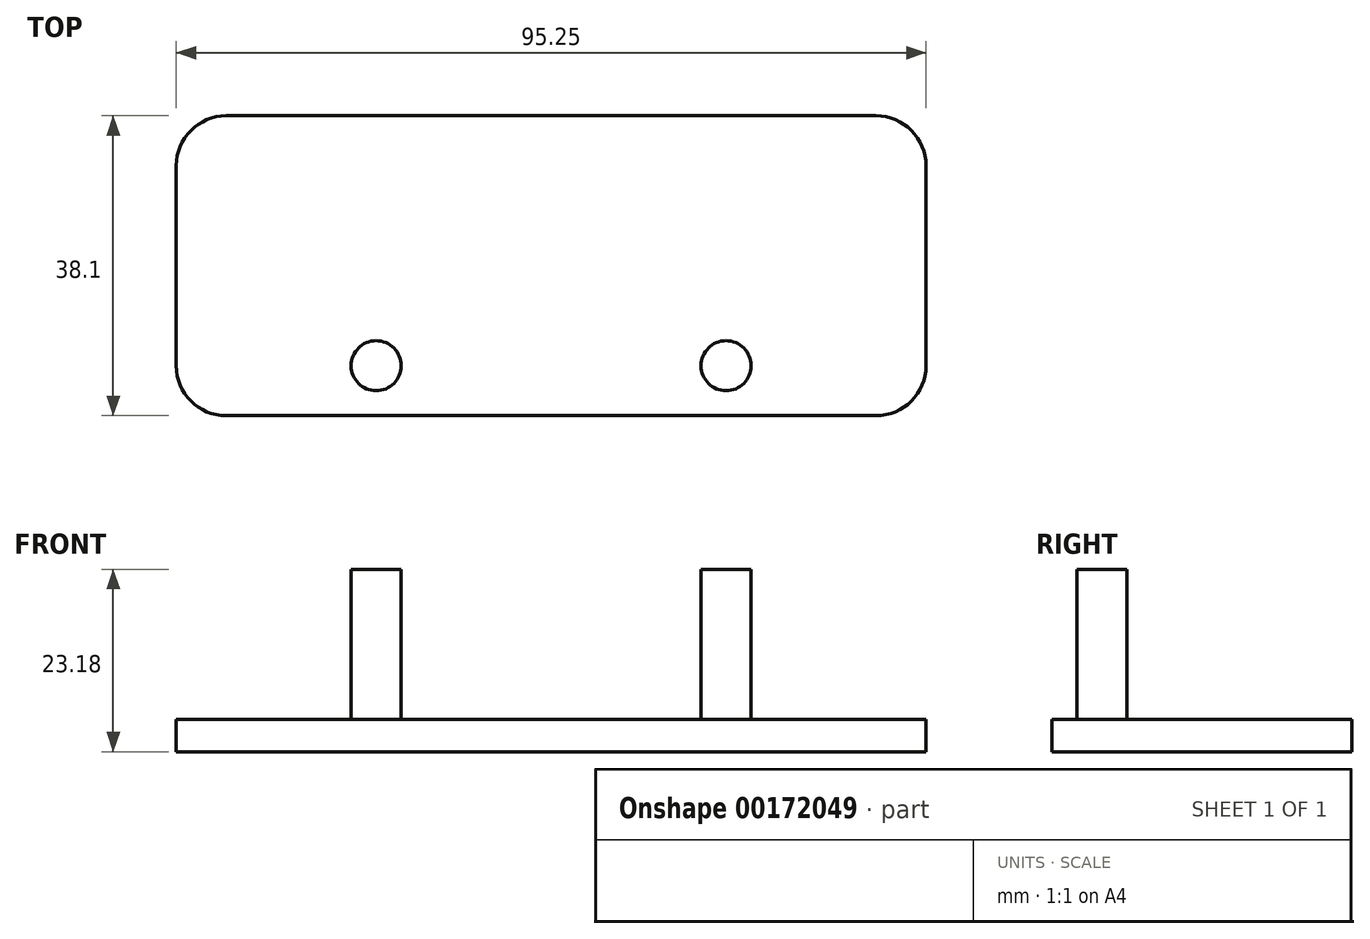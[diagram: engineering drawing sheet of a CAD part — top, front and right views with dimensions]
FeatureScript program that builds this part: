
annotation { "Feature Type Name" : "Feature", "Feature Type Description" : "" }
export const myFeature = defineFeature(function(context is Context, id is Id, definition is map)
    precondition{}
    {
        {
            var Q0;
            Q0=qCreatedBy(makeId("Top.planeOp"),FACE);
            var sketch = newSketch(context, id + "F0", { "sketchPlane" : qUnion([Q0])});
            skLineSegment(sketch, "E0.bottom", {"start": v(6.35, 0) * mm, "end": v(88.9, 0) * mm});
            skLineSegment(sketch, "E0.top", {"start": v(6.35, 38.1) * mm, "end": v(88.9, 38.1) * mm});
            skLineSegment(sketch, "E0.left", {"start": v(0, 6.35) * mm, "end": v(0, 31.75) * mm});
            skLineSegment(sketch, "E0.right", {"start": v(95.25, 6.35) * mm, "end": v(95.25, 31.75) * mm});
            skPoint(sketch, "E1.visualSharp", {"position": v(0, 38.1) * mm});
            skArc(sketch, "E1.filletArc", {"start": v(6.35, 38.1) * mm, "mid": v(1.86, 36.24) * mm, "end": v(0, 31.75) * mm});
            skPoint(sketch, "E2.visualSharp", {"position": v(0, 0) * mm});
            skArc(sketch, "E2.filletArc", {"start": v(0, 6.35) * mm, "mid": v(1.86, 1.86) * mm, "end": v(6.35, 0) * mm});
            skPoint(sketch, "E3.visualSharp", {"position": v(95.25, 38.1) * mm});
            skArc(sketch, "E3.filletArc", {"start": v(95.25, 31.75) * mm, "mid": v(93.4, 36.24) * mm, "end": v(88.9, 38.1) * mm});
            skPoint(sketch, "E4.visualSharp", {"position": v(95.25, 0) * mm});
            skArc(sketch, "E4.filletArc", {"start": v(88.9, 0) * mm, "mid": v(93.4, 1.86) * mm, "end": v(95.25, 6.35) * mm});
            skSolve(sketch);
        }
        {
            var Q0;
            Q0=makeQuery(id+"F0.imprint","IMPRINT",FACE,{"disambiguationData":[TD([[makeQuery(id+"F0.imprint","IMPRINT",EDGE,{"derivedFrom":sQuery(id+"F0.wireOp",EDGE,"E0.bottom")}),1.0]])]});
            extrude(context, id + "F1", {"entities" : qUnion([Q0]), "depth" : 4.13 * mm});
        }
        {
            var Q0;
            Q0=makeQuery(id+"F1.opExtrude","CAP_FACE",FACE,{"disambiguationData":[OSD([sQuery(id+"F0.wireOp",EDGE,"E0.bottom"),sQuery(id+"F0.wireOp",EDGE,"E0.top"),sQuery(id+"F0.wireOp",EDGE,"E0.left"),sQuery(id+"F0.wireOp",EDGE,"E0.right"),sQuery(id+"F0.wireOp",EDGE,"E1.filletArc"),sQuery(id+"F0.wireOp",EDGE,"E2.filletArc"),sQuery(id+"F0.wireOp",EDGE,"E3.filletArc"),sQuery(id+"F0.wireOp",EDGE,"E4.filletArc")])],"isStart":false});
            var sketch = newSketch(context, id + "F2", { "sketchPlane" : qUnion([Q0])});
            skCircle(sketch, "E5", {"center": v(25.4, 6.35) * mm, "radius": 3.18 * mm});
            skCircle(sketch, "E6", {"center": v(69.85, 6.35) * mm, "radius": 3.18 * mm});
            skSolve(sketch);
        }
        {
            var Q0;
            Q0=makeQuery(id+"F2.imprint","IMPRINT",FACE,{"disambiguationData":[TD([[makeQuery(id+"F2.imprint","IMPRINT",EDGE,{"derivedFrom":sQuery(id+"F2.wireOp",EDGE,"E5")}),1.0]])]});
            var Q1;
            Q1=makeQuery(id+"F2.imprint","IMPRINT",FACE,{"disambiguationData":[TD([[makeQuery(id+"F2.imprint","IMPRINT",EDGE,{"derivedFrom":sQuery(id+"F2.wireOp",EDGE,"E6")}),1.0]])]});
            extrude(context, id + "F3", {"entities" : qUnion([Q0, Q1]), "operationType" : NewBodyOperationType.ADD, "depth" : 19.05 * mm});
        }
    });
